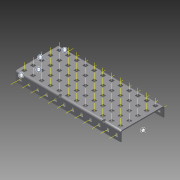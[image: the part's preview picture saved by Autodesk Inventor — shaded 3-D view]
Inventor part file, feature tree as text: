
AUTODESK INVENTOR PART (.ipt)
format: ipt  version: 2015 (Build 190159000, 159)  size: 2,557,440 bytes
history: native  units: in
note: dims shown in document units (in); Inventor stores cm internally (conversion verified against a paired STEP export)
features: other x90, pattern_linear x2, sheet_metal_op x1, extrude x1, imported_body x1, sketch x1
ambient origin geometry x8: Origin, YZ Plane, XZ Plane, XY Plane, X Axis, Y Axis, Z Axis, Center Point
bodies: Body1 (feature_tree)
feature tree (96):
  sheet_metal_op  "Fold1"
  other  "C-Channel"
  extrude  "length cut"  Depth=0.5in
  other  "top axis"
  other  "front axis"
  other  "back axis"
  pattern_linear  "top axes"  Spacing1=0.5in  [1 undecoded]
  pattern_linear  "horiz axes"  Spacing1=0.0in  [1 undecoded]
  other  "right plane"
  imported_body  "Base1"
  sketch  "Sketch1"  dims[d1=0.0in d4=0.5in d5=1.9685in d7=0.5in d10=0.5in d11=0.0in d12=0.0in d13=0.0in d14=-6.0in d15=0.0in d16=0.0in]
  other  "Work Point1"
  other  "Work Axis6"
  other  "Work Axis11"
  other  "Work Axis16"
  other  "Work Axis21"
  other  "Work Point2"
  other  "Work Point3"
  other  "Work Axis36"
  other  "Work Axis37"
  other  "Work Axis38"
  other  "Work Axis39"
  other  "Work Axis40"
  other  "Work Axis41"
  other  "Work Axis60"
  other  "Work Axis61"
  other  "Work Axis62"
  other  "Work Axis63"
  other  "Work Axis64"
  other  "Work Axis65"
  other  "Work Axis84"
  other  "Work Axis85"
  other  "Work Axis86"
  other  "Work Axis87"
  other  "Work Axis88"
  other  "Work Axis89"
  other  "Work Axis108"
  other  "Work Axis109"
  other  "Work Axis110"
  other  "Work Axis111"
  other  "Work Axis112"
  other  "Work Axis113"
  other  "Work Axis132"
  other  "Work Axis133"
  other  "Work Axis134"
  other  "Work Axis135"
  other  "Work Axis136"
  other  "Work Axis137"
  other  "Work Axis156"
  other  "Work Axis157"
  other  "Work Axis158"
  other  "Work Axis159"
  other  "Work Axis160"
  other  "Work Axis161"
  other  "Work Axis180"
  other  "Work Axis181"
  other  "Work Axis182"
  other  "Work Axis183"
  other  "Work Axis184"
  other  "Work Axis185"
  other  "Work Axis204"
  other  "Work Axis205"
  other  "Work Axis206"
  other  "Work Axis232"
  other  "Work Axis233"
  other  "Work Axis234"
  other  "Work Axis260"
  other  "Work Axis261"
  other  "Work Axis262"
  other  "Work Axis288"
  other  "Work Axis289"
  other  "Work Axis290"
  other  "Work Axis316"
  other  "Work Axis317"
  other  "Work Axis318"
  other  "Work Axis344"
  other  "Work Axis345"
  other  "Work Axis346"
  other  "Work Axis372"
  other  "Work Axis373"
  other  "Work Axis374"
  other  "left plane"
  other  "Work Axis400"
  other  "Work Axis401"
  other  "Work Axis402"
  other  "Work Axis403"
  other  "Work Axis404"
  other  "Work Axis405"
  other  "Work Axis406"
  other  "Work Axis407"
  other  "Work Axis408"
  other  "Work Axis409"
  other  "Work Axis410"
  other  "Work Axis411"
  other  "Work Axis412"
  other  "Work Axis413"
note: 2 required parameter values undecoded (feature->parameter linkage not recoverable at this tier; creation-order binding heuristic only, values carry confidence <= 0.55)
